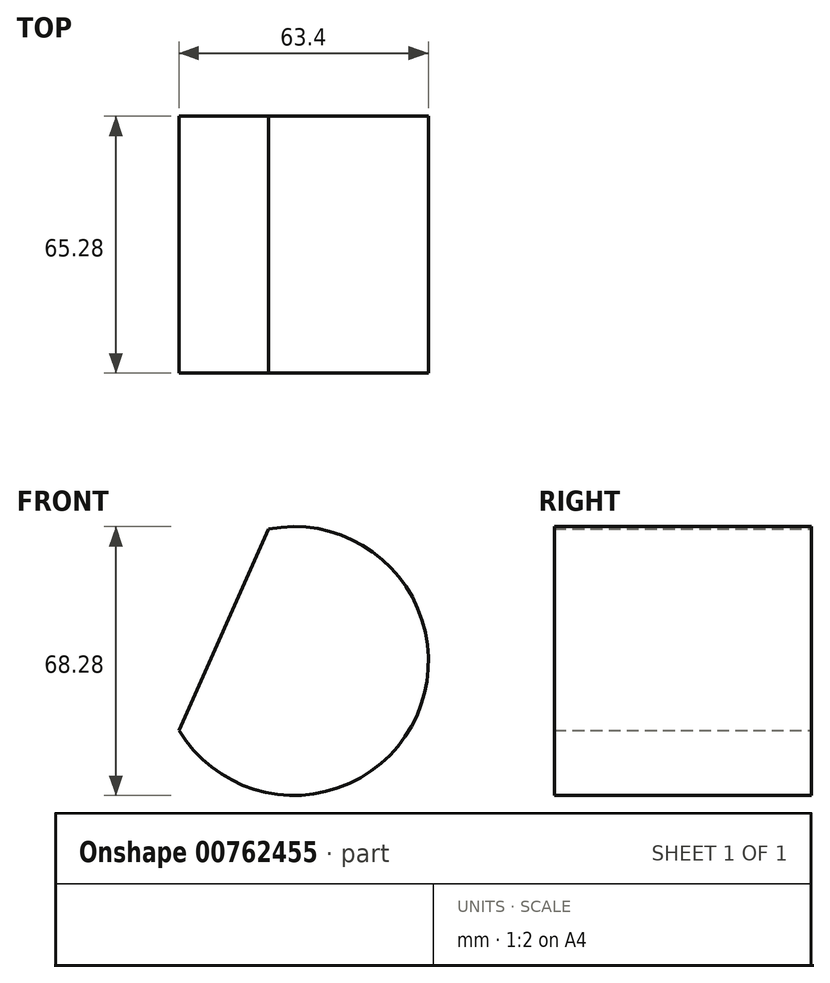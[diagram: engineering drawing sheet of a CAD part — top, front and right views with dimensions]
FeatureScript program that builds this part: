
annotation { "Feature Type Name" : "Feature", "Feature Type Description" : "" }
export const myFeature = defineFeature(function(context is Context, id is Id, definition is map)
    precondition{}
    {
        {
            var Q0;
            Q0=qCreatedBy(makeId("Front.planeOp"),FACE);
            var sketch = newSketch(context, id + "F0", { "sketchPlane" : qUnion([Q0])});
            skArc(sketch, "E0", {"start": v(-30.22, -20) * mm, "mid": v(30.22, -16.31) * mm, "end": v(-7.44, 31.1) * mm});
            skLineSegment(sketch, "E1", {"start": v(-7.44, 31.1) * mm, "end": v(-30.22, -20) * mm});
            skSolve(sketch);
        }
        {
            var Q0;
            Q0=makeQuery(id+"F0.imprint","IMPRINT",FACE,{"disambiguationData":[TD([[makeQuery(id+"F0.imprint","IMPRINT",EDGE,{"derivedFrom":sQuery(id+"F0.wireOp",EDGE,"E0")}),1.0]])]});
            extrude(context, id + "F1", {"entities" : qUnion([Q0]), "depth" : 65.28 * mm, "offsetDistance" : 25.4 * mm});
        }
    });
